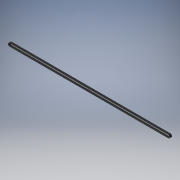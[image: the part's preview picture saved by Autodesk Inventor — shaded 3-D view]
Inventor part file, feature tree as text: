
AUTODESK INVENTOR PART (.ipt)
format: ipt  version: 2019 (Build 230136000, 136)  size: 169,984 bytes
history: native  units: mm
features: extrude x2
ambient origin geometry x8: Origin, YZ Plane, XZ Plane, XY Plane, X Axis, Y Axis, Z Axis, Center Point
bodies: Solid1 (feature_tree)
feature tree (2):
  extrude  "Extrusion1"  Depth=6.0mm TaperAngle=0.0deg
  extrude  "Extrusion2"  Depth=6.0mm TaperAngle=0.0deg
